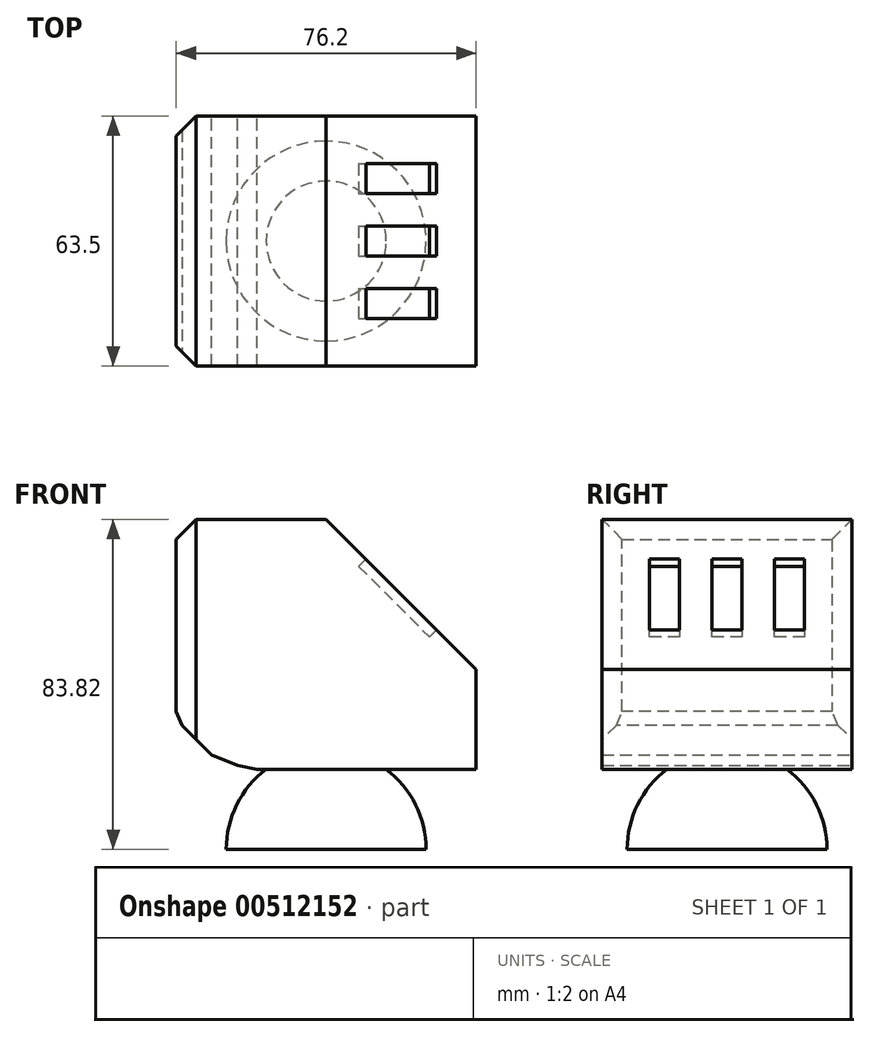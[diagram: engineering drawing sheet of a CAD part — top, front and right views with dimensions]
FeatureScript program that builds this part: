
annotation { "Feature Type Name" : "Feature", "Feature Type Description" : "" }
export const myFeature = defineFeature(function(context is Context, id is Id, definition is map)
    precondition{}
    {
        {
            var Q0;
            Q0=qCreatedBy(makeId("Top.planeOp"),FACE);
            var sketch = newSketch(context, id + "F0", { "sketchPlane" : qUnion([Q0])});
            skArc(sketch, "E0", {"start": v(0, -25.4) * mm, "mid": v(25.4, 0) * mm, "end": v(0, 25.4) * mm});
            skLineSegment(sketch, "E1", {"start": v(0, 25.4) * mm, "end": v(0, -25.4) * mm});
            skSolve(sketch);
        }
        {
            var Q0;
            Q0=makeQuery(id+"F0.imprint","IMPRINT",FACE,{"disambiguationData":[TD([[makeQuery(id+"F0.imprint","IMPRINT",EDGE,{"derivedFrom":sQuery(id+"F0.wireOp",EDGE,"E0")}),1.0]])]});
            var Q1;
            Q1=sQuery(id+"F0.wireOp",EDGE,"E1");
            revolve(context, id + "F1", {"entities" : qUnion([Q0]), "axis" : qUnion([Q1]), "revolveType" : RevolveType.ONE_DIRECTION, "angle" : 180 * degree});
        }
        {
            var Q0;
            Q0=qCreatedBy(makeId("Top.planeOp"),FACE);
            cPlane(context, id + "F2", {"entities" : qUnion([Q0]), "cplaneType" : CPlaneType.OFFSET, "offset" : 20.32 * mm, "width" : 152.4 * mm, "height" : 152.4 * mm});
        }
        {
            var Q0;
            Q0=qCreatedBy(id+"F2.planeOp",FACE);
            var sketch = newSketch(context, id + "F3", { "sketchPlane" : qUnion([Q0])});
            skLineSegment(sketch, "E2.bottom", {"start": v(38.1, 31.75) * mm, "end": v(-38.1, 31.75) * mm});
            skLineSegment(sketch, "E2.top", {"start": v(38.1, -31.75) * mm, "end": v(-38.1, -31.75) * mm});
            skLineSegment(sketch, "E2.left", {"start": v(38.1, 31.75) * mm, "end": v(38.1, -31.75) * mm});
            skLineSegment(sketch, "E2.right", {"start": v(-38.1, 31.75) * mm, "end": v(-38.1, -31.75) * mm});
            skPoint(sketch, "E2.middle", {"position": v(0, 0) * mm});
            skSolve(sketch);
        }
        {
            var Q0;
            Q0=makeQuery(id+"F3.imprint","IMPRINT",FACE,{"disambiguationData":[TD([[makeQuery(id+"F3.imprint","IMPRINT",EDGE,{"derivedFrom":sQuery(id+"F3.wireOp",EDGE,"E2.bottom")}),1.0]])]});
            extrude(context, id + "F4", {"entities" : qUnion([Q0]), "operationType" : NewBodyOperationType.ADD, "depth" : 63.5 * mm});
        }
        {
            var Q0;
            Q0=makeQuery(id+"F4.opExtrude","CAP_EDGE",EDGE,{"disambiguationData":[OSD([sQuery(id+"F3.wireOp",EDGE,"E2.right")])],"isStart":true});
            chamfer(context, id + "F5", {"entities" : qUnion([Q0]), "width" : 12.7 * mm, "tangentPropagation" : true});
        }
        {
            var Q0;
            {var subQ0=sQuery(id+"F3.wireOp",EDGE,"E2.right");Q0=makeQuery(id+"F5.opChamfer","BLEND_EDGE",EDGE,{"blendedFrom":[makeQuery(id+"F4.opExtrude","CAP_EDGE",EDGE,{"disambiguationData":[OSD([subQ0])],"isStart":true}),makeQuery(id+"F4.opExtrude","CAP_FACE",FACE,{"disambiguationData":[OSD([sQuery(id+"F3.wireOp",EDGE,"E2.bottom"),sQuery(id+"F3.wireOp",EDGE,"E2.top"),sQuery(id+"F3.wireOp",EDGE,"E2.left"),subQ0])],"isStart":true})],"blendedInto":[makeQuery(id+"F4.opExtrude","CAP_FACE",FACE,{"disambiguationData":[OSD([sQuery(id+"F3.wireOp",EDGE,"E2.bottom"),sQuery(id+"F3.wireOp",EDGE,"E2.top"),sQuery(id+"F3.wireOp",EDGE,"E2.left"),subQ0])],"isStart":true})]});}
            chamfer(context, id + "F6", {"entities" : qUnion([Q0]), "width" : 12.7 * mm, "tangentPropagation" : true});
        }
        {
            var Q0;
            {var subQ0=sQuery(id+"F3.wireOp",EDGE,"E2.right");var subQ1=makeQuery(id+"F4.opExtrude","CAP_FACE",FACE,{"disambiguationData":[OSD([sQuery(id+"F3.wireOp",EDGE,"E2.bottom"),sQuery(id+"F3.wireOp",EDGE,"E2.top"),sQuery(id+"F3.wireOp",EDGE,"E2.left"),subQ0])],"isStart":true});Q0=makeQuery(id+"F6.opChamfer","BLEND_EDGE",EDGE,{"disambiguationData":[OD(0.0)],"blendedFrom":[makeQuery(id+"F5.opChamfer","BLEND_EDGE",EDGE,{"blendedFrom":[makeQuery(id+"F4.opExtrude","CAP_EDGE",EDGE,{"disambiguationData":[OSD([subQ0])],"isStart":true}),subQ1],"blendedInto":[subQ1]}),subQ1],"blendedInto":[subQ1]});}
            var Q1;
            {var subQ0=sQuery(id+"F3.wireOp",EDGE,"E2.right");var subQ1=makeQuery(id+"F4.opExtrude","CAP_FACE",FACE,{"disambiguationData":[OSD([sQuery(id+"F3.wireOp",EDGE,"E2.bottom"),sQuery(id+"F3.wireOp",EDGE,"E2.top"),sQuery(id+"F3.wireOp",EDGE,"E2.left"),subQ0])],"isStart":true});Q1=makeQuery(id+"F6.opChamfer","BLEND_EDGE",EDGE,{"disambiguationData":[OD(1.0)],"blendedFrom":[makeQuery(id+"F5.opChamfer","BLEND_EDGE",EDGE,{"blendedFrom":[makeQuery(id+"F4.opExtrude","CAP_EDGE",EDGE,{"disambiguationData":[OSD([subQ0])],"isStart":true}),subQ1],"blendedInto":[subQ1]}),subQ1],"blendedInto":[subQ1]});}
            chamfer(context, id + "F7", {"entities" : qUnion([Q0, Q1]), "width" : 12.7 * mm, "tangentPropagation" : true});
        }
        {
            var Q0;
            Q0=makeQuery(id+"F4.opExtrude","SWEPT_EDGE",EDGE,{"disambiguationData":[OSD([sQuery(id+"F3.wireOp",EDGE,"E2.bottom"),sQuery(id+"F3.wireOp",EDGE,"E2.right")])]});
            var Q1;
            Q1=makeQuery(id+"F4.opExtrude","CAP_EDGE",EDGE,{"disambiguationData":[OSD([sQuery(id+"F3.wireOp",EDGE,"E2.right")])],"isStart":false});
            var Q2;
            Q2=makeQuery(id+"F4.opExtrude","SWEPT_EDGE",EDGE,{"disambiguationData":[OSD([sQuery(id+"F3.wireOp",EDGE,"E2.top"),sQuery(id+"F3.wireOp",EDGE,"E2.right")])]});
            var Q3;
            {var subQ0=sQuery(id+"F3.wireOp",EDGE,"E2.right");Q3=makeQuery(id+"F5.opChamfer","BLEND_EDGE",EDGE,{"blendedFrom":[makeQuery(id+"F4.opExtrude","CAP_EDGE",EDGE,{"disambiguationData":[OSD([subQ0])],"isStart":true}),makeQuery(id+"F4.opExtrude","SWEPT_FACE",FACE,{"disambiguationData":[OSD([subQ0])]})],"blendedInto":[makeQuery(id+"F4.opExtrude","SWEPT_FACE",FACE,{"disambiguationData":[OSD([subQ0])]})]});}
            chamfer(context, id + "F8", {"entities" : qUnion([Q0, Q1, Q2, Q3]), "width" : 5.08 * mm, "tangentPropagation" : true});
        }
        {
            var Q0;
            Q0=makeQuery(id+"F4.opExtrude","CAP_EDGE",EDGE,{"disambiguationData":[OSD([sQuery(id+"F3.wireOp",EDGE,"E2.left")])],"isStart":false});
            chamfer(context, id + "F9", {"entities" : qUnion([Q0]), "width" : 38.1 * mm, "tangentPropagation" : true});
        }
        {
            var Q0;
            Q0=makeQuery(id+"F9.opChamfer","BLEND_FACE",FACE,{"disambiguationData":[OSD([sQuery(id+"F3.wireOp",EDGE,"E2.left")])]});
            var sketch = newSketch(context, id + "F10", { "sketchPlane" : qUnion([Q0])});
            skLineSegment(sketch, "E3", {"start": v(-31.75, 32.33) * mm, "end": v(31.75, 32.33) * mm, "construction": true});
            skLineSegment(sketch, "E4", {"start": v(31.75, 32.33) * mm, "end": v(0, 32.33) * mm, "construction": true});
            skLineSegment(sketch, "E5", {"start": v(0, 32.33) * mm, "end": v(-31.75, 32.33) * mm, "construction": true});
            skLineSegment(sketch, "E6.bottom", {"start": v(-12.06, 45.03) * mm, "end": v(-19.68, 45.03) * mm});
            skLineSegment(sketch, "E6.top", {"start": v(-12.06, 19.63) * mm, "end": v(-19.68, 19.63) * mm});
            skLineSegment(sketch, "E6.left", {"start": v(-12.06, 45.03) * mm, "end": v(-12.06, 19.63) * mm});
            skLineSegment(sketch, "E6.right", {"start": v(-19.68, 45.03) * mm, "end": v(-19.68, 19.63) * mm});
            skPoint(sketch, "E6.middle", {"position": v(-15.87, 32.33) * mm});
            skLineSegment(sketch, "E7.bottom", {"start": v(3.81, 45.03) * mm, "end": v(-3.8, 45.03) * mm});
            skLineSegment(sketch, "E7.top", {"start": v(3.81, 19.63) * mm, "end": v(-3.8, 19.63) * mm});
            skLineSegment(sketch, "E7.left", {"start": v(3.81, 45.03) * mm, "end": v(3.81, 19.63) * mm});
            skLineSegment(sketch, "E7.right", {"start": v(-3.8, 45.03) * mm, "end": v(-3.8, 19.63) * mm});
            skPoint(sketch, "E7.middle", {"position": v(0, 32.33) * mm});
            skLineSegment(sketch, "E8.bottom", {"start": v(19.69, 45.03) * mm, "end": v(12.07, 45.03) * mm});
            skLineSegment(sketch, "E8.top", {"start": v(19.69, 19.63) * mm, "end": v(12.07, 19.63) * mm});
            skLineSegment(sketch, "E8.left", {"start": v(19.69, 45.03) * mm, "end": v(19.69, 19.63) * mm});
            skLineSegment(sketch, "E8.right", {"start": v(12.07, 45.03) * mm, "end": v(12.07, 19.63) * mm});
            skPoint(sketch, "E8.middle", {"position": v(15.88, 32.33) * mm});
            skSolve(sketch);
        }
        {
            var Q0;
            Q0=makeQuery(id+"F10.imprint","IMPRINT",FACE,{"disambiguationData":[TD([[makeQuery(id+"F10.imprint","IMPRINT",EDGE,{"derivedFrom":sQuery(id+"F10.wireOp",EDGE,"E8.bottom")}),1.0]])]});
            var Q1;
            Q1=makeQuery(id+"F10.imprint","IMPRINT",FACE,{"disambiguationData":[TD([[makeQuery(id+"F10.imprint","IMPRINT",EDGE,{"derivedFrom":sQuery(id+"F10.wireOp",EDGE,"E7.bottom")}),1.0]])]});
            var Q2;
            Q2=makeQuery(id+"F10.imprint","IMPRINT",FACE,{"disambiguationData":[TD([[makeQuery(id+"F10.imprint","IMPRINT",EDGE,{"derivedFrom":sQuery(id+"F10.wireOp",EDGE,"E6.bottom")}),1.0]])]});
            extrude(context, id + "F11", {"entities" : qUnion([Q0, Q1, Q2]), "operationType" : NewBodyOperationType.REMOVE, "oppositeDirection" : true, "depth" : 2.54 * mm});
        }
    });
